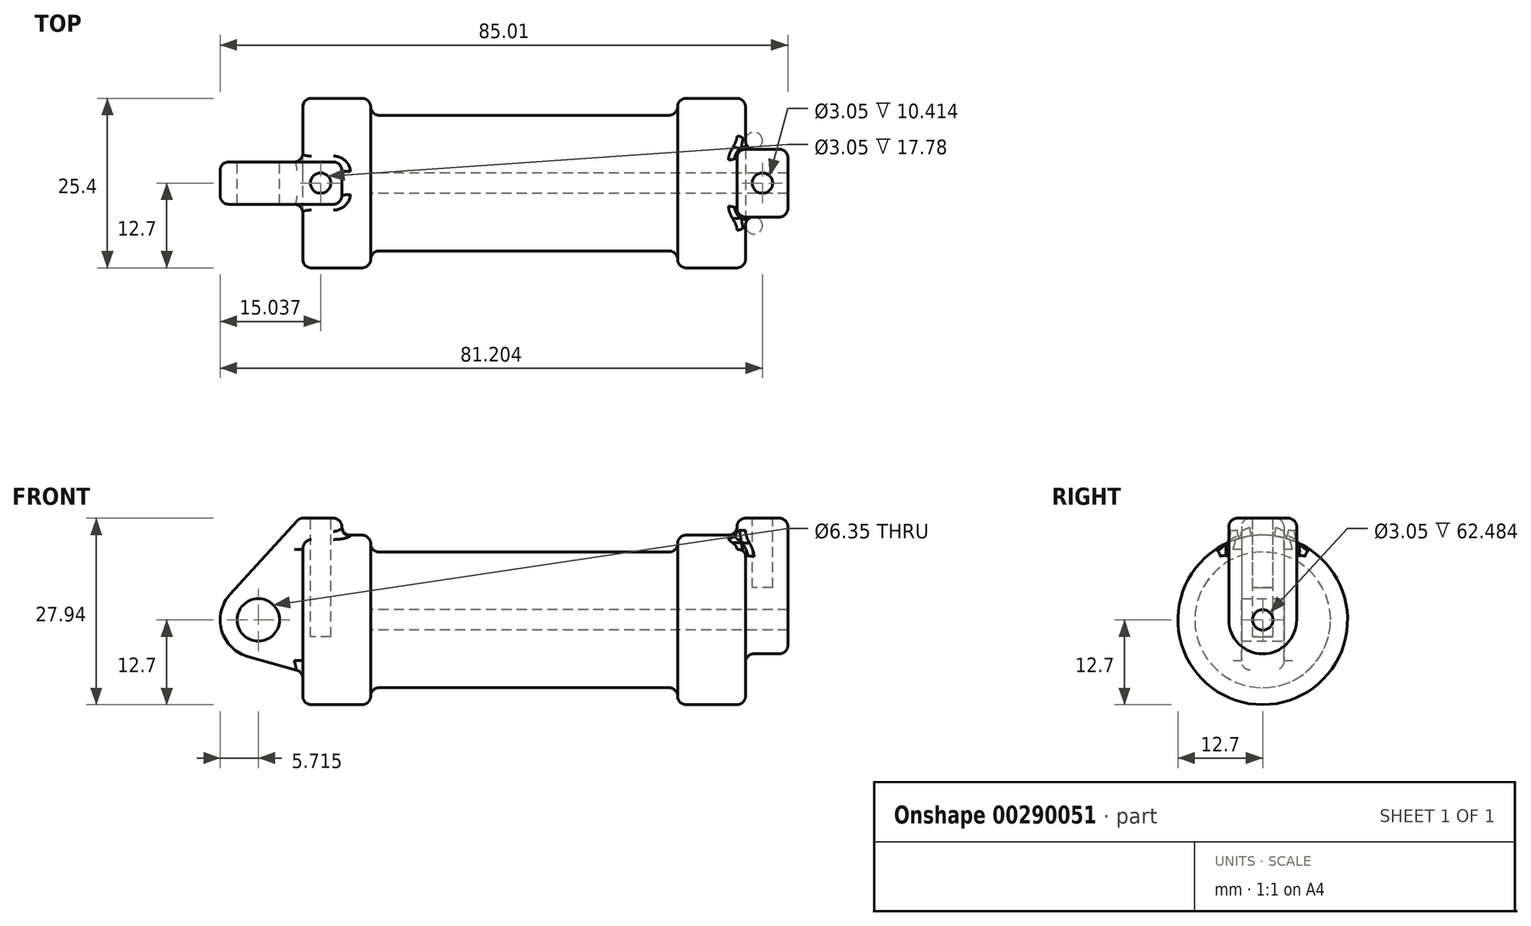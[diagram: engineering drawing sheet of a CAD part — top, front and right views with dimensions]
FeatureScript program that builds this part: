
annotation { "Feature Type Name" : "Feature", "Feature Type Description" : "" }
export const myFeature = defineFeature(function(context is Context, id is Id, definition is map)
    precondition{}
    {
        {
            var Q0;
            Q0=qCreatedBy(makeId("Front.planeOp"),FACE);
            var sketch = newSketch(context, id + "F0", { "sketchPlane" : qUnion([Q0])});
            skLineSegment(sketch, "E0", {"start": v(0, 0) * mm, "end": v(0, 12.7) * mm});
            skLineSegment(sketch, "E1", {"start": v(0, 12.7) * mm, "end": v(10.16, 12.7) * mm});
            skLineSegment(sketch, "E2", {"start": v(10.16, 12.7) * mm, "end": v(10.16, 10.16) * mm});
            skLineSegment(sketch, "E3", {"start": v(10.16, 10.16) * mm, "end": v(56.13, 10.16) * mm});
            skLineSegment(sketch, "E4", {"start": v(56.13, 10.16) * mm, "end": v(56.13, 12.7) * mm});
            skLineSegment(sketch, "E5", {"start": v(56.13, 12.7) * mm, "end": v(66.3, 12.7) * mm});
            skLineSegment(sketch, "E6", {"start": v(66.3, 12.7) * mm, "end": v(66.3, 0) * mm});
            skLineSegment(sketch, "E7", {"start": v(66.3, 0) * mm, "end": v(0, 0) * mm});
            skLineSegment(sketch, "E8", {"start": v(5.84, 15.24) * mm, "end": v(-0.5, 15.24) * mm});
            skLineSegment(sketch, "E9", {"start": v(-0.5, 15.24) * mm, "end": v(-10.88, 3.85) * mm});
            skLineSegment(sketch, "E10", {"start": v(0, 0) * mm, "end": v(-6.65, 0) * mm});
            skCircle(sketch, "E11", {"center": v(-6.65, 0) * mm, "radius": 5.72 * mm});
            skCircle(sketch, "E12", {"center": v(-6.65, 0) * mm, "radius": 3.18 * mm});
            skLineSegment(sketch, "E13", {"start": v(5.84, 15.24) * mm, "end": v(5.84, -9.4) * mm});
            skLineSegment(sketch, "E14", {"start": v(5.84, -9.4) * mm, "end": v(-8.18, -5.5) * mm});
            skSolve(sketch);
        }
        {
            var Q0;
            {var subQ0=sQuery(id+"F0.wireOp",EDGE,"E2");Q0=makeQuery(id+"F0.imprint","IMPRINT",FACE,{"disambiguationData":[TD([[makeQuery(id+"F0.imprint","IMPRINT",EDGE,{"derivedFrom":subQ0}),-1.0]])]});}
            var Q1;
            {var subQ0=sQuery(id+"F0.wireOp",EDGE,"E0");Q1=makeQuery(id+"F0.imprint","IMPRINT",FACE,{"disambiguationData":[TD([[makeQuery(id+"F0.imprint","IMPRINT",EDGE,{"derivedFrom":subQ0}),-1.0]])]});}
            var Q2;
            Q2=sQuery(id+"F0.wireOp",EDGE,"E7");
            revolve(context, id + "F1", {"entities" : qUnion([Q0, Q1]), "axis" : qUnion([Q2]), "revolveType" : RevolveType.FULL});
        }
        {
            var Q0;
            {var subQ1=sQuery(id+"F0.wireOp",EDGE,"E0");Q0=makeQuery(id+"F0.imprint","IMPRINT",FACE,{"disambiguationData":[TD([[makeQuery(id+"F0.imprint","IMPRINT",EDGE,{"derivedFrom":subQ1}),1.0]])]});}
            var Q1;
            Q1=makeQuery(id+"F0.imprint","IMPRINT",FACE,{"disambiguationData":[TD([[makeQuery(id+"F0.imprint","IMPRINT",EDGE,{"derivedFrom":sQuery(id+"F0.wireOp",EDGE,"E12")}),-1.0]])]});
            var Q2;
            {var subQ0=sQuery(id+"F0.wireOp",EDGE,"E14");Q2=makeQuery(id+"F0.imprint","IMPRINT",FACE,{"disambiguationData":[TD([[makeQuery(id+"F0.imprint","IMPRINT",EDGE,{"derivedFrom":subQ0}),-1.0]])]});}
            var Q3;
            {var subQ0=sQuery(id+"F0.wireOp",EDGE,"E0");Q3=makeQuery(id+"F0.imprint","IMPRINT",FACE,{"disambiguationData":[TD([[makeQuery(id+"F0.imprint","IMPRINT",EDGE,{"derivedFrom":subQ0}),-1.0]])]});}
            extrude(context, id + "F2", {"entities" : qUnion([Q0, Q1, Q2, Q3]), "operationType" : NewBodyOperationType.ADD, "endBound" : BoundingType.SYMMETRIC, "depth" : 6.35 * mm});
        }
        {
            var Q0;
            Q0=makeQuery(id+"F1.opRevolve","SWEPT_FACE",FACE,{"disambiguationData":[OSD([sQuery(id+"F0.wireOp",EDGE,"E6")])]});
            var sketch = newSketch(context, id + "F3", { "sketchPlane" : qUnion([Q0])});
            skCircle(sketch, "E15", {"center": v(0, 0) * mm, "radius": 1.52 * mm});
            skCircle(sketch, "E16", {"center": v(0, 0) * mm, "radius": 5.08 * mm});
            skLineSegment(sketch, "E17", {"start": v(-5.08, 0) * mm, "end": v(-5.08, 15.24) * mm});
            skLineSegment(sketch, "E18", {"start": v(5.08, 0) * mm, "end": v(5.08, 15.24) * mm});
            skLineSegment(sketch, "E19", {"start": v(-5.08, 15.24) * mm, "end": v(5.08, 15.24) * mm});
            skSolve(sketch);
        }
        {
            var Q0;
            {var subQ0=sQuery(id+"F3.wireOp",EDGE,"E17");var subQ1=sQuery(id+"F3.wireOp",EDGE,"E16");var subQ2=makeQuery(id+"F3.imprint","INTERSECT",VERTEX,{"derivedFrom":[subQ1,subQ0]});Q0=makeQuery(id+"F3.imprint","IMPRINT",FACE,{"disambiguationData":[TD([[makeQuery(id+"F3.imprint","IMPRINT",EDGE,{"disambiguationData":[TD([[subQ2,1.0]])],"derivedFrom":subQ1}),-1.0]])]});}
            var Q1;
            {var subQ0=sQuery(id+"F3.wireOp",EDGE,"E19");Q1=makeQuery(id+"F3.imprint","IMPRINT",FACE,{"disambiguationData":[TD([[makeQuery(id+"F3.imprint","IMPRINT",EDGE,{"derivedFrom":subQ0}),-1.0]])]});}
            var Q2;
            Q2=makeQuery(id+"F3.imprint","IMPRINT",FACE,{"disambiguationData":[TD([[makeQuery(id+"F3.imprint","IMPRINT",EDGE,{"derivedFrom":sQuery(id+"F3.wireOp",EDGE,"E15")}),-1.0]])]});
            extrude(context, id + "F4", {"entities" : qUnion([Q0, Q1, Q2]), "operationType" : NewBodyOperationType.ADD, "depth" : 6.35 * mm, "hasSecondDirection" : true, "secondDirectionOppositeDirection" : true, "secondDirectionDepth" : 1.27 * mm});
        }
        {
            var Q0;
            Q0=makeQuery(id+"F3.imprint","IMPRINT",FACE,{"disambiguationData":[TD([[makeQuery(id+"F3.imprint","IMPRINT",EDGE,{"derivedFrom":sQuery(id+"F3.wireOp",EDGE,"E15")}),1.0]])]});
            var Q1;
            Q1=makeQuery(id+"F1.opRevolve","SWEPT_FACE",FACE,{"disambiguationData":[OSD([sQuery(id+"F0.wireOp",EDGE,"E2")])]});
            extrude(context, id + "F5", {"entities" : qUnion([Q0]), "operationType" : NewBodyOperationType.REMOVE, "endBound" : BoundingType.UP_TO_SURFACE, "oppositeDirection" : true, "endBoundEntityFace" : qUnion([Q1]), "depth" : 50.8 * mm});
        }
        {
            var Q0;
            {var subQ0=sQuery(id+"F3.wireOp",EDGE,"E19");Q0=makeQuery(id+"F4.boolean.opBoolean","MERGE",FACE,{"derivedFrom":[makeQuery(id+"FMD7mD6K4aEccil_1.opExtrude","SWEPT_FACE",FACE,{"disambiguationData":[OSD([subQ0])]}),makeQuery(id+"F4.opExtrude","SWEPT_FACE",FACE,{"disambiguationData":[OSD([subQ0])]})]});}
            var sketch = newSketch(context, id + "F6", { "sketchPlane" : qUnion([Q0])});
            skCircle(sketch, "E20", {"center": v(68.83, 0) * mm, "radius": 1.52 * mm});
            skLineSegment(sketch, "E21", {"start": v(72.64, 0) * mm, "end": v(68.83, 0) * mm, "construction": true});
            skSolve(sketch);
        }
        {
            var Q0;
            Q0=makeQuery(id+"F2.opExtrude","SWEPT_FACE",FACE,{"disambiguationData":[OSD([sQuery(id+"F0.wireOp",EDGE,"E8")])]});
            var sketch = newSketch(context, id + "F7", { "sketchPlane" : qUnion([Q0])});
            skLineSegment(sketch, "E22", {"start": v(5.84, 0) * mm, "end": v(2.67, 0) * mm, "construction": true});
            skCircle(sketch, "E23", {"center": v(2.67, 0) * mm, "radius": 1.52 * mm});
            skSolve(sketch);
        }
        {
            var Q0;
            Q0=makeQuery(id+"F6.imprint","IMPRINT",FACE,{"disambiguationData":[TD([[makeQuery(id+"F6.imprint","IMPRINT",EDGE,{"derivedFrom":sQuery(id+"F6.wireOp",EDGE,"E20")}),1.0]])]});
            var Q1;
            Q1=sQuery(id+"F6.wireOp",EDGE,"E20");
            extrude(context, id + "F8", {"entities" : qUnion([Q0]), "operationType" : NewBodyOperationType.REMOVE, "surfaceEntities" : qUnion([Q1]), "oppositeDirection" : true, "depth" : 10.4 * mm});
        }
        {
            var Q0;
            Q0=makeQuery(id+"F7.imprint","IMPRINT",FACE,{"disambiguationData":[TD([[makeQuery(id+"F7.imprint","IMPRINT",EDGE,{"derivedFrom":sQuery(id+"F7.wireOp",EDGE,"E23")}),1.0]])]});
            var Q1;
            Q1=sQuery(id+"F7.wireOp",EDGE,"E23");
            extrude(context, id + "F9", {"entities" : qUnion([Q0]), "operationType" : NewBodyOperationType.REMOVE, "surfaceEntities" : qUnion([Q1]), "oppositeDirection" : true, "depth" : 17.78 * mm});
        }
        {
            var Q0;
            Q0=makeQuery(id+"F1.opRevolve","SWEPT_EDGE",EDGE,{"disambiguationData":[OSD([sQuery(id+"F0.wireOp",EDGE,"E2"),sQuery(id+"F0.wireOp",EDGE,"E3")])]});
            var Q1;
            Q1=makeQuery(id+"F1.opRevolve","SWEPT_EDGE",EDGE,{"disambiguationData":[OSD([sQuery(id+"F0.wireOp",EDGE,"E1"),sQuery(id+"F0.wireOp",EDGE,"E2")])]});
            var Q2;
            Q2=makeQuery(id+"F2.opExtrude","CAP_EDGE",EDGE,{"disambiguationData":[OSD([sQuery(id+"F0.wireOp",EDGE,"E13")])],"isStart":true});
            var Q3;
            Q3=makeQuery(id+"F2.opExtrude","SWEPT_EDGE",EDGE,{"disambiguationData":[OSD([sQuery(id+"F0.wireOp",EDGE,"E8"),sQuery(id+"F0.wireOp",EDGE,"E13")])]});
            var Q4;
            Q4=makeQuery(id+"F2.boolean.opBoolean","INTERSECT",EDGE,{"derivedFrom":[makeQuery(id+"F1.opRevolve","SWEPT_FACE",FACE,{"disambiguationData":[OSD([sQuery(id+"F0.wireOp",EDGE,"E1")])]}),makeQuery(id+"F2.opExtrude","SWEPT_FACE",FACE,{"disambiguationData":[OSD([sQuery(id+"F0.wireOp",EDGE,"E13")])]})]});
            var Q5;
            Q5=makeQuery(id+"F2.boolean.opBoolean","INTERSECT",EDGE,{"derivedFrom":[makeQuery(id+"F1.opRevolve","SWEPT_FACE",FACE,{"disambiguationData":[OSD([sQuery(id+"F0.wireOp",EDGE,"E1")])]}),makeQuery(id+"F2.opExtrude","CAP_FACE",FACE,{"disambiguationData":[OSD([sQuery(id+"F0.wireOp",EDGE,"E8"),sQuery(id+"F0.wireOp",EDGE,"E9"),sQuery(id+"F0.wireOp",EDGE,"E11"),sQuery(id+"F0.wireOp",EDGE,"E12"),sQuery(id+"F0.wireOp",EDGE,"E13"),sQuery(id+"F0.wireOp",EDGE,"E14")])],"isStart":true})]});
            var Q6;
            Q6=makeQuery(id+"F2.opExtrude","CAP_EDGE",EDGE,{"disambiguationData":[OSD([sQuery(id+"F0.wireOp",EDGE,"E8")])],"isStart":true});
            var Q7;
            Q7=makeQuery(id+"F2.opExtrude","CAP_EDGE",EDGE,{"disambiguationData":[OSD([sQuery(id+"F0.wireOp",EDGE,"E8")])],"isStart":false});
            var Q8;
            Q8=makeQuery(id+"F2.opExtrude","CAP_EDGE",EDGE,{"disambiguationData":[OSD([sQuery(id+"F0.wireOp",EDGE,"E13")])],"isStart":false});
            var Q9;
            Q9=makeQuery(id+"F1.opRevolve","SWEPT_EDGE",EDGE,{"disambiguationData":[OSD([sQuery(id+"F0.wireOp",EDGE,"E0"),sQuery(id+"F0.wireOp",EDGE,"E1")])]});
            var Q10;
            Q10=makeQuery(id+"F2.opExtrude","SWEPT_EDGE",EDGE,{"disambiguationData":[OSD([sQuery(id+"F0.wireOp",EDGE,"E8"),sQuery(id+"F0.wireOp",EDGE,"E9")])]});
            var Q11;
            Q11=makeQuery(id+"F2.opExtrude","CAP_EDGE",EDGE,{"disambiguationData":[OSD([sQuery(id+"F0.wireOp",EDGE,"E11")])],"isStart":true});
            var Q12;
            Q12=makeQuery(id+"F2.opExtrude","CAP_EDGE",EDGE,{"disambiguationData":[OSD([sQuery(id+"F0.wireOp",EDGE,"E14")])],"isStart":true});
            var Q13;
            Q13=makeQuery(id+"F2.boolean.opBoolean","INTERSECT",EDGE,{"derivedFrom":[makeQuery(id+"F1.opRevolve","SWEPT_FACE",FACE,{"disambiguationData":[OSD([sQuery(id+"F0.wireOp",EDGE,"E0")])]}),makeQuery(id+"F2.opExtrude","CAP_FACE",FACE,{"disambiguationData":[OSD([sQuery(id+"F0.wireOp",EDGE,"E8"),sQuery(id+"F0.wireOp",EDGE,"E9"),sQuery(id+"F0.wireOp",EDGE,"E11"),sQuery(id+"F0.wireOp",EDGE,"E12"),sQuery(id+"F0.wireOp",EDGE,"E13"),sQuery(id+"F0.wireOp",EDGE,"E14")])],"isStart":true})]});
            var Q14;
            Q14=makeQuery(id+"F2.boolean.opBoolean","INTERSECT",EDGE,{"derivedFrom":[makeQuery(id+"F1.opRevolve","SWEPT_FACE",FACE,{"disambiguationData":[OSD([sQuery(id+"F0.wireOp",EDGE,"E0")])]}),makeQuery(id+"F2.opExtrude","SWEPT_FACE",FACE,{"disambiguationData":[OSD([sQuery(id+"F0.wireOp",EDGE,"E14")])]})]});
            var Q15;
            Q15=makeQuery(id+"F2.opExtrude","CAP_EDGE",EDGE,{"disambiguationData":[OSD([sQuery(id+"F0.wireOp",EDGE,"E11")])],"isStart":false});
            var Q16;
            Q16=makeQuery(id+"F2.opExtrude","CAP_EDGE",EDGE,{"disambiguationData":[OSD([sQuery(id+"F0.wireOp",EDGE,"E9")])],"isStart":true});
            var Q17;
            Q17=makeQuery(id+"F2.opExtrude","CAP_EDGE",EDGE,{"disambiguationData":[OSD([sQuery(id+"F0.wireOp",EDGE,"E9")])],"isStart":false});
            var Q18;
            Q18=makeQuery(id+"F2.opExtrude","CAP_EDGE",EDGE,{"disambiguationData":[OSD([sQuery(id+"F0.wireOp",EDGE,"E14")])],"isStart":false});
            var Q19;
            Q19=makeQuery(id+"F2.boolean.opBoolean","INTERSECT",EDGE,{"derivedFrom":[makeQuery(id+"F1.opRevolve","SWEPT_FACE",FACE,{"disambiguationData":[OSD([sQuery(id+"F0.wireOp",EDGE,"E0")])]}),makeQuery(id+"F2.opExtrude","CAP_FACE",FACE,{"disambiguationData":[OSD([sQuery(id+"F0.wireOp",EDGE,"E8"),sQuery(id+"F0.wireOp",EDGE,"E9"),sQuery(id+"F0.wireOp",EDGE,"E11"),sQuery(id+"F0.wireOp",EDGE,"E12"),sQuery(id+"F0.wireOp",EDGE,"E13"),sQuery(id+"F0.wireOp",EDGE,"E14")])],"isStart":false})]});
            var Q20;
            Q20=makeQuery(id+"F2.boolean.opBoolean","INTERSECT",EDGE,{"derivedFrom":[makeQuery(id+"F1.opRevolve","SWEPT_FACE",FACE,{"disambiguationData":[OSD([sQuery(id+"F0.wireOp",EDGE,"E1")])]}),makeQuery(id+"F2.opExtrude","CAP_FACE",FACE,{"disambiguationData":[OSD([sQuery(id+"F0.wireOp",EDGE,"E8"),sQuery(id+"F0.wireOp",EDGE,"E9"),sQuery(id+"F0.wireOp",EDGE,"E11"),sQuery(id+"F0.wireOp",EDGE,"E12"),sQuery(id+"F0.wireOp",EDGE,"E13"),sQuery(id+"F0.wireOp",EDGE,"E14")])],"isStart":false})]});
            fillet(context, id + "F10", {"entities" : qUnion([Q0, Q1, Q2, Q3, Q4, Q5, Q6, Q7, Q8, Q9, Q10, Q11, Q12, Q13, Q14, Q15, Q16, Q17, Q18, Q19, Q20]), "radius" : 1.27 * mm, "tangentPropagation" : true, "allowEdgeOverflow" : false});
        }
        {
            var Q0;
            {var subQ0=sQuery(id+"F3.wireOp",EDGE,"E19");var subQ1=sQuery(id+"F3.wireOp",EDGE,"E18");Q0=makeQuery(id+"F4.boolean.opBoolean","MERGE",EDGE,{"derivedFrom":[makeQuery(id+"FMD7mD6K4aEccil_1.opExtrude","SWEPT_EDGE",EDGE,{"disambiguationData":[OSD([subQ1,subQ0])]}),makeQuery(id+"F4.opExtrude","SWEPT_EDGE",EDGE,{"disambiguationData":[OSD([subQ1,subQ0])]})]});}
            var Q1;
            Q1=makeQuery(id+"F4.opExtrude","CAP_EDGE",EDGE,{"disambiguationData":[OSD([sQuery(id+"F3.wireOp",EDGE,"E19")])],"isStart":false});
            var Q2;
            {var subQ0=sQuery(id+"F3.wireOp",EDGE,"E19");var subQ1=sQuery(id+"F3.wireOp",EDGE,"E17");Q2=makeQuery(id+"F4.boolean.opBoolean","MERGE",EDGE,{"derivedFrom":[makeQuery(id+"FMD7mD6K4aEccil_1.opExtrude","SWEPT_EDGE",EDGE,{"disambiguationData":[OSD([subQ1,subQ0])]}),makeQuery(id+"F4.opExtrude","SWEPT_EDGE",EDGE,{"disambiguationData":[OSD([subQ1,subQ0])]})]});}
            var Q3;
            Q3=makeQuery(id+"F1.opRevolve","SWEPT_EDGE",EDGE,{"disambiguationData":[OSD([sQuery(id+"F0.wireOp",EDGE,"E4"),sQuery(id+"F0.wireOp",EDGE,"E5")])]});
            var Q4;
            Q4=makeQuery(id+"F1.opRevolve","SWEPT_EDGE",EDGE,{"disambiguationData":[OSD([sQuery(id+"F0.wireOp",EDGE,"E3"),sQuery(id+"F0.wireOp",EDGE,"E4")])]});
            var Q5;
            Q5=makeQuery(id+"FMD7mD6K4aEccil_1.opExtrude","CAP_EDGE",EDGE,{"disambiguationData":[OSD([sQuery(id+"F3.wireOp",EDGE,"E19")])],"isStart":false});
            var Q6;
            Q6=makeQuery(id+"F4.opExtrude","CAP_EDGE",EDGE,{"disambiguationData":[OSD([sQuery(id+"F3.wireOp",EDGE,"E17")])],"isStart":false});
            var Q7;
            Q7=makeQuery(id+"F4.opExtrude","CAP_EDGE",EDGE,{"disambiguationData":[OSD([sQuery(id+"F3.wireOp",EDGE,"E16")])],"isStart":false});
            var Q8;
            Q8=makeQuery(id+"F1.opRevolve","SWEPT_EDGE",EDGE,{"disambiguationData":[OSD([sQuery(id+"F0.wireOp",EDGE,"E5"),sQuery(id+"F0.wireOp",EDGE,"E6")])]});
            var Q9;
            Q9=makeQuery(id+"F4.opExtrude","CAP_EDGE",EDGE,{"disambiguationData":[OSD([sQuery(id+"F3.wireOp",EDGE,"E17")])],"isStart":true});
            var Q10;
            Q10=makeQuery(id+"F4.opExtrude","CAP_EDGE",EDGE,{"disambiguationData":[OSD([sQuery(id+"F3.wireOp",EDGE,"E18")])],"isStart":true});
            var Q11;
            Q11=makeQuery(id+"F4.opExtrude","CAP_EDGE",EDGE,{"disambiguationData":[OSD([sQuery(id+"F3.wireOp",EDGE,"E18")])],"isStart":false});
            var Q12;
            Q12=makeQuery(id+"F4.opExtrude","CAP_EDGE",EDGE,{"disambiguationData":[OSD([sQuery(id+"F3.wireOp",EDGE,"E19")])],"isStart":true});
            var Q13;
            Q13=makeQuery(id+"F4.boolean.opBoolean","INTERSECT",EDGE,{"derivedFrom":[makeQuery(id+"F1.opRevolve","SWEPT_FACE",FACE,{"disambiguationData":[OSD([sQuery(id+"F0.wireOp",EDGE,"E5")])]}),makeQuery(id+"F4.opExtrude","CAP_FACE",FACE,{"disambiguationData":[OSD([sQuery(id+"F3.wireOp",EDGE,"E15"),sQuery(id+"F3.wireOp",EDGE,"E16"),sQuery(id+"F3.wireOp",EDGE,"E17"),sQuery(id+"F3.wireOp",EDGE,"E18"),sQuery(id+"F3.wireOp",EDGE,"E19")])],"isStart":true})]});
            var Q14;
            Q14=makeQuery(id+"F4.boolean.opBoolean","INTERSECT",EDGE,{"derivedFrom":[makeQuery(id+"F1.opRevolve","SWEPT_FACE",FACE,{"disambiguationData":[OSD([sQuery(id+"F0.wireOp",EDGE,"E5")])]}),makeQuery(id+"F4.opExtrude","SWEPT_FACE",FACE,{"disambiguationData":[OSD([sQuery(id+"F3.wireOp",EDGE,"E17")])]})]});
            var Q15;
            Q15=makeQuery(id+"F4.boolean.opBoolean","INTERSECT",EDGE,{"derivedFrom":[makeQuery(id+"F1.opRevolve","SWEPT_FACE",FACE,{"disambiguationData":[OSD([sQuery(id+"F0.wireOp",EDGE,"E6")])]}),makeQuery(id+"F4.opExtrude","SWEPT_FACE",FACE,{"disambiguationData":[OSD([sQuery(id+"F3.wireOp",EDGE,"E17")])]})]});
            var Q16;
            Q16=makeQuery(id+"F4.boolean.opBoolean","INTERSECT",EDGE,{"derivedFrom":[makeQuery(id+"F1.opRevolve","SWEPT_FACE",FACE,{"disambiguationData":[OSD([sQuery(id+"F0.wireOp",EDGE,"E6")])]}),makeQuery(id+"F4.opExtrude","SWEPT_FACE",FACE,{"disambiguationData":[OSD([sQuery(id+"F3.wireOp",EDGE,"E16")])]})]});
            var Q17;
            Q17=makeQuery(id+"F4.boolean.opBoolean","INTERSECT",EDGE,{"derivedFrom":[makeQuery(id+"F1.opRevolve","SWEPT_FACE",FACE,{"disambiguationData":[OSD([sQuery(id+"F0.wireOp",EDGE,"E6")])]}),makeQuery(id+"F4.opExtrude","SWEPT_FACE",FACE,{"disambiguationData":[OSD([sQuery(id+"F3.wireOp",EDGE,"E18")])]})]});
            var Q18;
            Q18=makeQuery(id+"F4.boolean.opBoolean","INTERSECT",EDGE,{"derivedFrom":[makeQuery(id+"F1.opRevolve","SWEPT_FACE",FACE,{"disambiguationData":[OSD([sQuery(id+"F0.wireOp",EDGE,"E5")])]}),makeQuery(id+"F4.opExtrude","SWEPT_FACE",FACE,{"disambiguationData":[OSD([sQuery(id+"F3.wireOp",EDGE,"E18")])]})]});
            fillet(context, id + "F11", {"entities" : qUnion([Q0, Q1, Q2, Q3, Q4, Q5, Q6, Q7, Q8, Q9, Q10, Q11, Q12, Q13, Q14, Q15, Q16, Q17, Q18]), "radius" : 1.27 * mm, "tangentPropagation" : true, "allowEdgeOverflow" : false});
        }
    });
